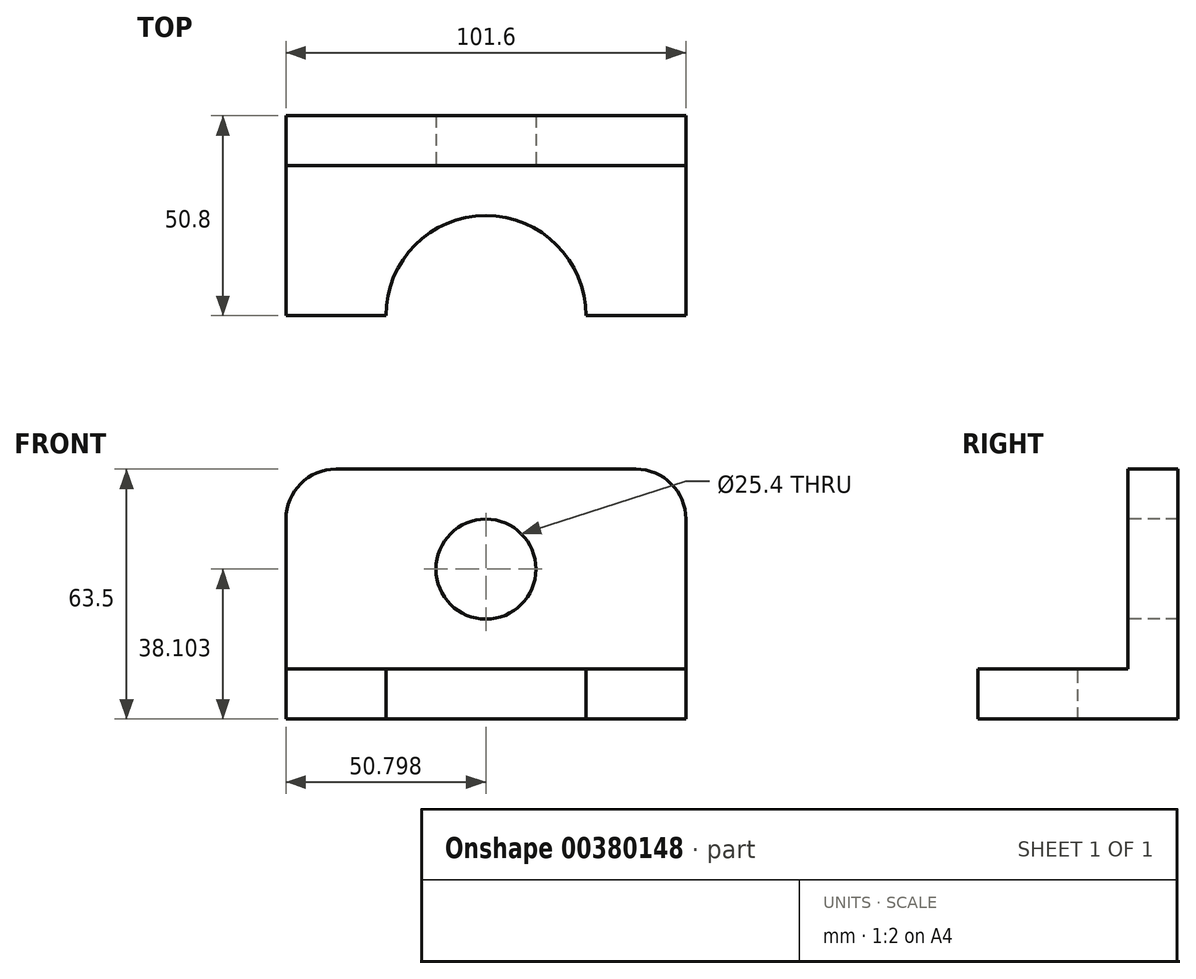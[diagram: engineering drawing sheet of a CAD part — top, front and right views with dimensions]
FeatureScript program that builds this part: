
annotation { "Feature Type Name" : "Feature", "Feature Type Description" : "" }
export const myFeature = defineFeature(function(context is Context, id is Id, definition is map)
    precondition{}
    {
        {
            var Q0;
            Q0=qCreatedBy(makeId("Front.planeOp"),FACE);
            var sketch = newSketch(context, id + "F0", { "sketchPlane" : qUnion([Q0])});
            skLineSegment(sketch, "E0.bottom", {"start": v(-28.11, 62.95) * mm, "end": v(73.49, 62.95) * mm});
            skLineSegment(sketch, "E0.top", {"start": v(-28.11, -0.55) * mm, "end": v(73.49, -0.55) * mm});
            skLineSegment(sketch, "E0.left", {"start": v(-28.11, 62.95) * mm, "end": v(-28.11, -0.55) * mm});
            skLineSegment(sketch, "E0.right", {"start": v(73.49, 62.95) * mm, "end": v(73.49, -0.55) * mm});
            skSolve(sketch);
        }
        {
            var Q0;
            Q0=makeQuery(id+"F0.imprint","IMPRINT",FACE,{"disambiguationData":[TD([[makeQuery(id+"F0.imprint","IMPRINT",EDGE,{"derivedFrom":sQuery(id+"F0.wireOp",EDGE,"E0.bottom")}),-1.0]])]});
            var Q1;
            Q1 = qSketchRegion(id + "F0", true);
            extrude(context, id + "F1", {"entities" : qUnion([Q0, Q1]), "depth" : 50.8 * mm});
        }
        {
            var Q0;
            Q0=makeQuery(id+"F1.opExtrude","SWEPT_FACE",FACE,{"disambiguationData":[OSD([sQuery(id+"F0.wireOp",EDGE,"E0.right")])]});
            var sketch = newSketch(context, id + "F2", { "sketchPlane" : qUnion([Q0])});
            skLineSegment(sketch, "E1.bottom", {"start": v(-76.2, 88.35) * mm, "end": v(-12.7, 88.35) * mm});
            skLineSegment(sketch, "E1.top", {"start": v(-76.2, 12.15) * mm, "end": v(-12.7, 12.15) * mm});
            skLineSegment(sketch, "E1.left", {"start": v(-76.2, 88.35) * mm, "end": v(-76.2, 12.15) * mm});
            skLineSegment(sketch, "E1.right", {"start": v(-12.7, 88.35) * mm, "end": v(-12.7, 12.15) * mm});
            skSolve(sketch);
        }
        {
            var Q0;
            Q0 = qSketchRegion(id + "F2", true);
            extrude(context, id + "F3", {"entities" : qUnion([Q0]), "operationType" : NewBodyOperationType.REMOVE, "endBound" : BoundingType.THROUGH_ALL, "oppositeDirection" : true, "depth" : 25.4 * mm});
        }
        {
            var Q0;
            Q0=makeQuery(id+"F3.boolean.opBoolean","COPY",FACE,{"derivedFrom":makeQuery(id+"F3.opExtrude","SWEPT_FACE",FACE,{"disambiguationData":[OSD([sQuery(id+"F2.wireOp",EDGE,"E1.right")])]})});
            var sketch = newSketch(context, id + "F4", { "sketchPlane" : qUnion([Q0])});
            skCircle(sketch, "E2", {"center": v(22.69, 37.55) * mm, "radius": 12.7 * mm});
            skPoint(sketch, "E2.centerSnap0", {"position": v(22.69, 12.15) * mm});
            skSolve(sketch);
        }
        {
            var Q0;
            Q0 = qSketchRegion(id + "F4", true);
            extrude(context, id + "F5", {"entities" : qUnion([Q0]), "operationType" : NewBodyOperationType.REMOVE, "endBound" : BoundingType.THROUGH_ALL, "oppositeDirection" : true, "depth" : 25.4 * mm});
        }
        {
            var Q0;
            Q0=makeQuery(id+"F3.boolean.opBoolean","COPY",FACE,{"derivedFrom":makeQuery(id+"F3.opExtrude","SWEPT_FACE",FACE,{"disambiguationData":[OSD([sQuery(id+"F2.wireOp",EDGE,"E1.top")])]})});
            var sketch = newSketch(context, id + "F6", { "sketchPlane" : qUnion([Q0])});
            skCircle(sketch, "E3", {"center": v(22.69, -50.8) * mm, "radius": 25.4 * mm});
            skSolve(sketch);
        }
        {
            var Q0;
            Q0 = qSketchRegion(id + "F6", true);
            extrude(context, id + "F7", {"entities" : qUnion([Q0]), "operationType" : NewBodyOperationType.REMOVE, "endBound" : BoundingType.THROUGH_ALL, "oppositeDirection" : true, "depth" : 25.4 * mm});
        }
        {
            var Q0;
            Q0=makeQuery(id+"F1.opExtrude","SWEPT_EDGE",EDGE,{"disambiguationData":[OSD([sQuery(id+"F0.wireOp",EDGE,"E0.bottom"),sQuery(id+"F0.wireOp",EDGE,"E0.left")])]});
            var Q1;
            Q1=makeQuery(id+"F1.opExtrude","SWEPT_EDGE",EDGE,{"disambiguationData":[OSD([sQuery(id+"F0.wireOp",EDGE,"E0.bottom"),sQuery(id+"F0.wireOp",EDGE,"E0.right")])]});
            fillet(context, id + "F8", {"entities" : qUnion([Q0, Q1]), "radius" : 12.7 * mm, "tangentPropagation" : true, "allowEdgeOverflow" : false});
        }
    });
